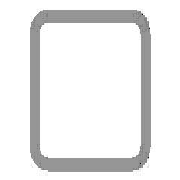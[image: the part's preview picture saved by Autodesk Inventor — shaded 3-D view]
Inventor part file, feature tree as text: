
AUTODESK INVENTOR PART (.ipt)
format: ipt  version: 2024 (Build 280153000, 153)  size: 128,512 bytes
history: native  units: mm (DEFAULTED — no unit token found)
features: other x4, extrude x1, sketch x1, plane x1
ambient origin geometry x8: Origin, YZ Plane, XZ Plane, XY Plane, X Axis, Y Axis, Z Axis, Center Point
bodies: Solid1 (feature_tree)
feature tree (7):
  parser-record x1  (decoder bookkeeping rows leaked as tree rows — omitted from the tree; the rows remain in map.json)
  other  "Driven Length"
  other  "Plano inicial"
  other  "Plano final"
  extrude  "Cuerpo"  TaperAngle=0.0deg  [1 undecoded]
  sketch  "Sketch3"  dims[d3=500.0mm d4=0.0mm d10=50.8mm d11=50.8mm d12=3.175mm d13=-0.0mm d14=500.0mm d15=25.4mm d16=25.4mm d17=6.35mm d18=90.0deg d19=500.0mm]
  plane  "Work Plane3"
note: 1 required parameter value undecoded (feature->parameter linkage not recoverable at this tier; creation-order binding heuristic only, values carry confidence <= 0.55)
